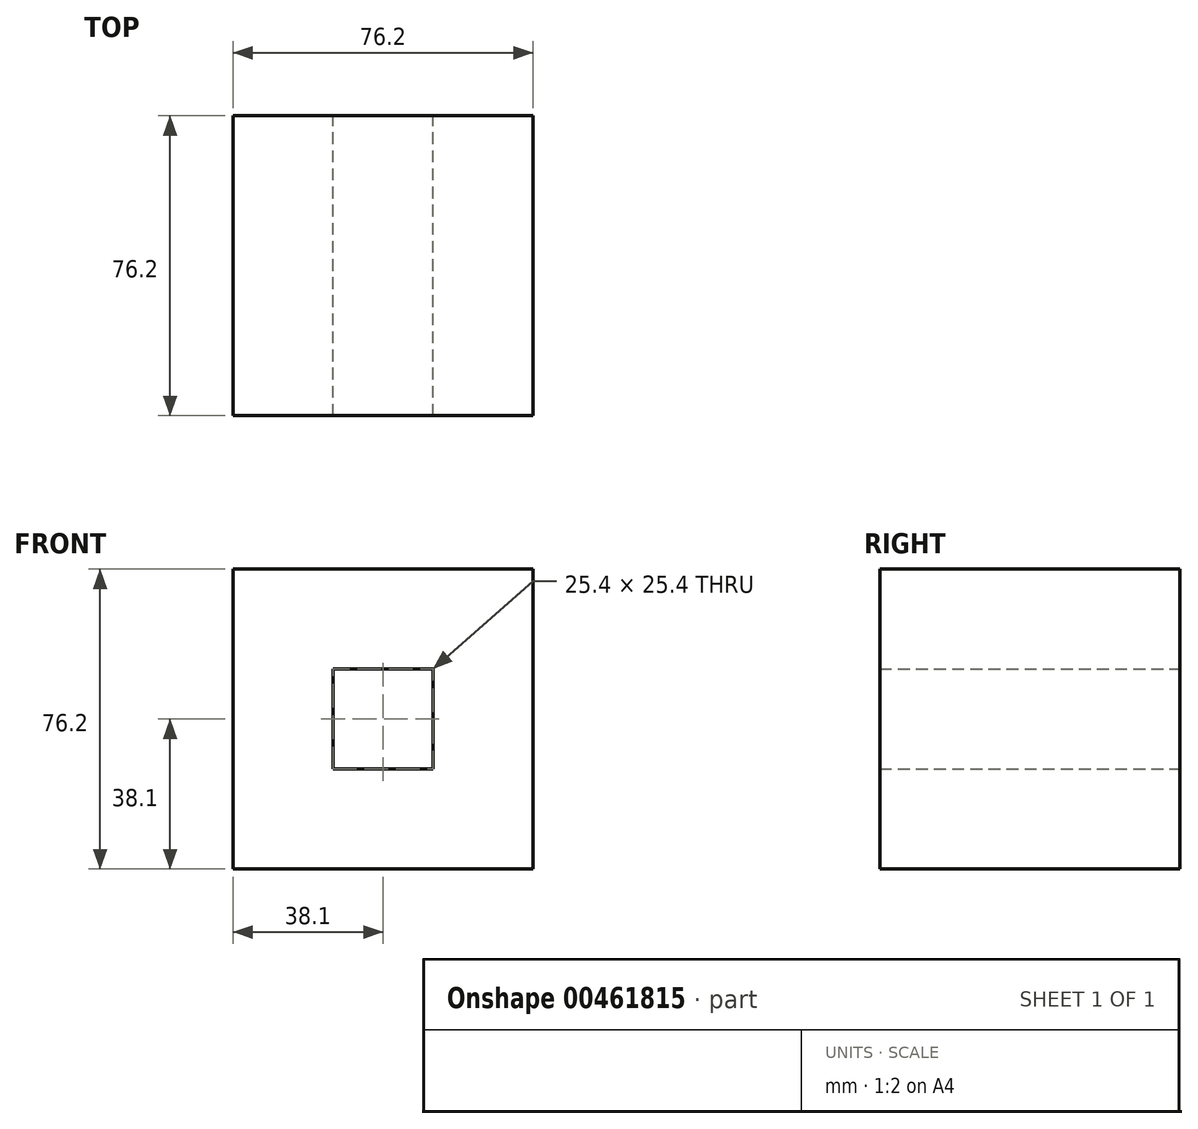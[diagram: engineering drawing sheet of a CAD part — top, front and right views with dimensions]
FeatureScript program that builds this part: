
annotation { "Feature Type Name" : "Feature", "Feature Type Description" : "" }
export const myFeature = defineFeature(function(context is Context, id is Id, definition is map)
    precondition{}
    {
        {
            var Q0;
            Q0=qCreatedBy(makeId("Front.planeOp"),FACE);
            var sketch = newSketch(context, id + "F0", { "sketchPlane" : qUnion([Q0])});
            skLineSegment(sketch, "E0.bottom", {"start": v(38.1, 38.1) * mm, "end": v(-38.1, 38.1) * mm});
            skLineSegment(sketch, "E0.top", {"start": v(38.1, -38.1) * mm, "end": v(-38.1, -38.1) * mm});
            skLineSegment(sketch, "E0.left", {"start": v(38.1, 38.1) * mm, "end": v(38.1, -38.1) * mm});
            skLineSegment(sketch, "E0.right", {"start": v(-38.1, 38.1) * mm, "end": v(-38.1, -38.1) * mm});
            skPoint(sketch, "E0.middle", {"position": v(0, 0) * mm});
            skSolve(sketch);
        }
        {
            var Q0;
            Q0 = qSketchRegion(id + "F0", true);
            extrude(context, id + "F1", {"entities" : qUnion([Q0]), "depth" : 76.2 * mm});
        }
        {
            var Q0;
            Q0=qCreatedBy(makeId("Front.planeOp"),FACE);
            var sketch = newSketch(context, id + "F2", { "sketchPlane" : qUnion([Q0])});
            skLineSegment(sketch, "E1.bottom", {"start": v(12.7, 12.7) * mm, "end": v(-12.7, 12.7) * mm});
            skLineSegment(sketch, "E1.top", {"start": v(12.7, -12.7) * mm, "end": v(-12.7, -12.7) * mm});
            skLineSegment(sketch, "E1.left", {"start": v(12.7, 12.7) * mm, "end": v(12.7, -12.7) * mm});
            skLineSegment(sketch, "E1.right", {"start": v(-12.7, 12.7) * mm, "end": v(-12.7, -12.7) * mm});
            skPoint(sketch, "E1.middle", {"position": v(0, 0) * mm});
            skSolve(sketch);
        }
        {
            var Q0;
            Q0 = qSketchRegion(id + "F2", true);
            extrude(context, id + "F3", {"entities" : qUnion([Q0]), "operationType" : NewBodyOperationType.REMOVE, "endBound" : BoundingType.THROUGH_ALL, "depth" : 25.4 * mm});
        }
    });
